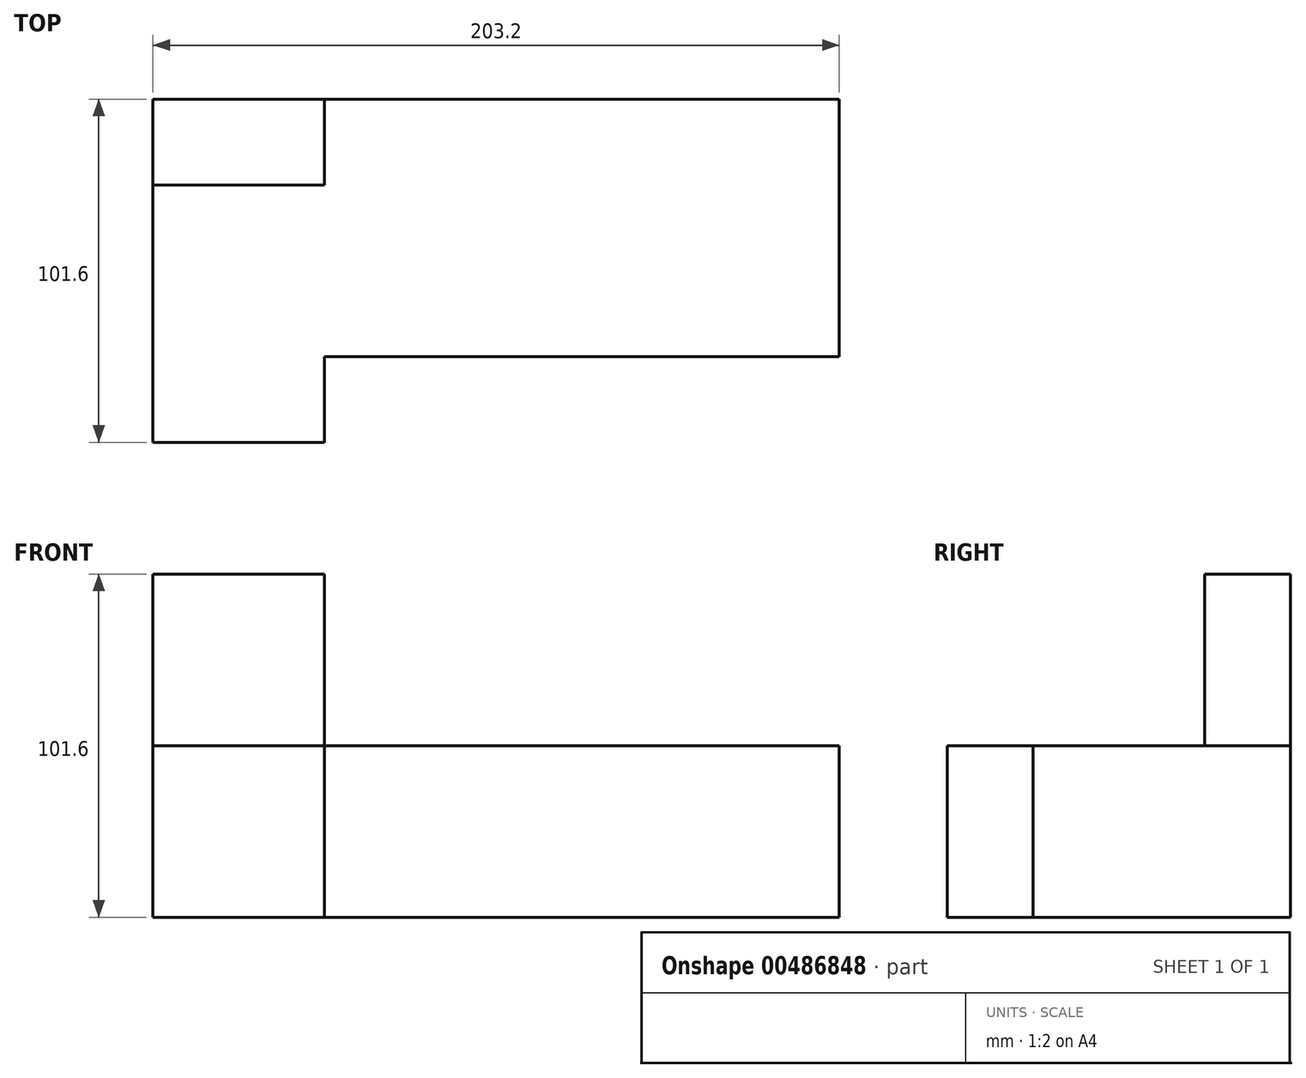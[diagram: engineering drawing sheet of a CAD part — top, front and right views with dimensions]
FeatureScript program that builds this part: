
annotation { "Feature Type Name" : "Feature", "Feature Type Description" : "" }
export const myFeature = defineFeature(function(context is Context, id is Id, definition is map)
    precondition{}
    {
        {
            var Q0;
            Q0=qCreatedBy(makeId("Top.planeOp"),FACE);
            var sketch = newSketch(context, id + "F0", { "sketchPlane" : qUnion([Q0])});
            skLineSegment(sketch, "E0.bottom", {"start": v(0, 0) * mm, "end": v(-203.2, 0) * mm});
            skLineSegment(sketch, "E0.top", {"start": v(0, 101.6) * mm, "end": v(-203.2, 101.6) * mm});
            skLineSegment(sketch, "E0.left", {"start": v(0, 0) * mm, "end": v(0, 101.6) * mm});
            skLineSegment(sketch, "E0.right", {"start": v(-203.2, 0) * mm, "end": v(-203.2, 101.6) * mm});
            skSolve(sketch);
        }
        {
            var Q0;
            Q0 = qSketchRegion(id + "F0", true);
            extrude(context, id + "F1", {"entities" : qUnion([Q0]), "depth" : 50.8 * mm});
        }
        {
            var Q0;
            Q0=makeQuery(id+"F1.opExtrude","CAP_FACE",FACE,{"disambiguationData":[OSD([sQuery(id+"F0.wireOp",EDGE,"E0.bottom"),sQuery(id+"F0.wireOp",EDGE,"E0.top"),sQuery(id+"F0.wireOp",EDGE,"E0.left"),sQuery(id+"F0.wireOp",EDGE,"E0.right")])],"isStart":false});
            var sketch = newSketch(context, id + "F2", { "sketchPlane" : qUnion([Q0])});
            skLineSegment(sketch, "E1.bottom", {"start": v(0, 0) * mm, "end": v(-152.4, 0) * mm});
            skLineSegment(sketch, "E1.top", {"start": v(0, 25.4) * mm, "end": v(-152.4, 25.4) * mm});
            skLineSegment(sketch, "E1.left", {"start": v(0, 0) * mm, "end": v(0, 25.4) * mm});
            skLineSegment(sketch, "E1.right", {"start": v(-152.4, 0) * mm, "end": v(-152.4, 25.4) * mm});
            skSolve(sketch);
        }
        {
            var Q0;
            Q0 = qSketchRegion(id + "F2", true);
            extrude(context, id + "F3", {"entities" : qUnion([Q0]), "operationType" : NewBodyOperationType.REMOVE, "oppositeDirection" : true, "depth" : 50.8 * mm});
        }
        {
            var Q0;
            Q0=makeQuery(id+"F1.opExtrude","CAP_FACE",FACE,{"disambiguationData":[OSD([sQuery(id+"F0.wireOp",EDGE,"E0.bottom"),sQuery(id+"F0.wireOp",EDGE,"E0.top"),sQuery(id+"F0.wireOp",EDGE,"E0.left"),sQuery(id+"F0.wireOp",EDGE,"E0.right")])],"isStart":false});
            var sketch = newSketch(context, id + "F4", { "sketchPlane" : qUnion([Q0])});
            skLineSegment(sketch, "E2.bottom", {"start": v(-203.2, 101.6) * mm, "end": v(-152.4, 101.6) * mm});
            skLineSegment(sketch, "E2.top", {"start": v(-203.2, 76.2) * mm, "end": v(-152.4, 76.2) * mm});
            skLineSegment(sketch, "E2.left", {"start": v(-203.2, 101.6) * mm, "end": v(-203.2, 76.2) * mm});
            skLineSegment(sketch, "E2.right", {"start": v(-152.4, 101.6) * mm, "end": v(-152.4, 76.2) * mm});
            skSolve(sketch);
        }
        {
            var Q0;
            Q0 = qSketchRegion(id + "F4", true);
            extrude(context, id + "F5", {"entities" : qUnion([Q0]), "operationType" : NewBodyOperationType.ADD, "depth" : 50.8 * mm});
        }
    });
